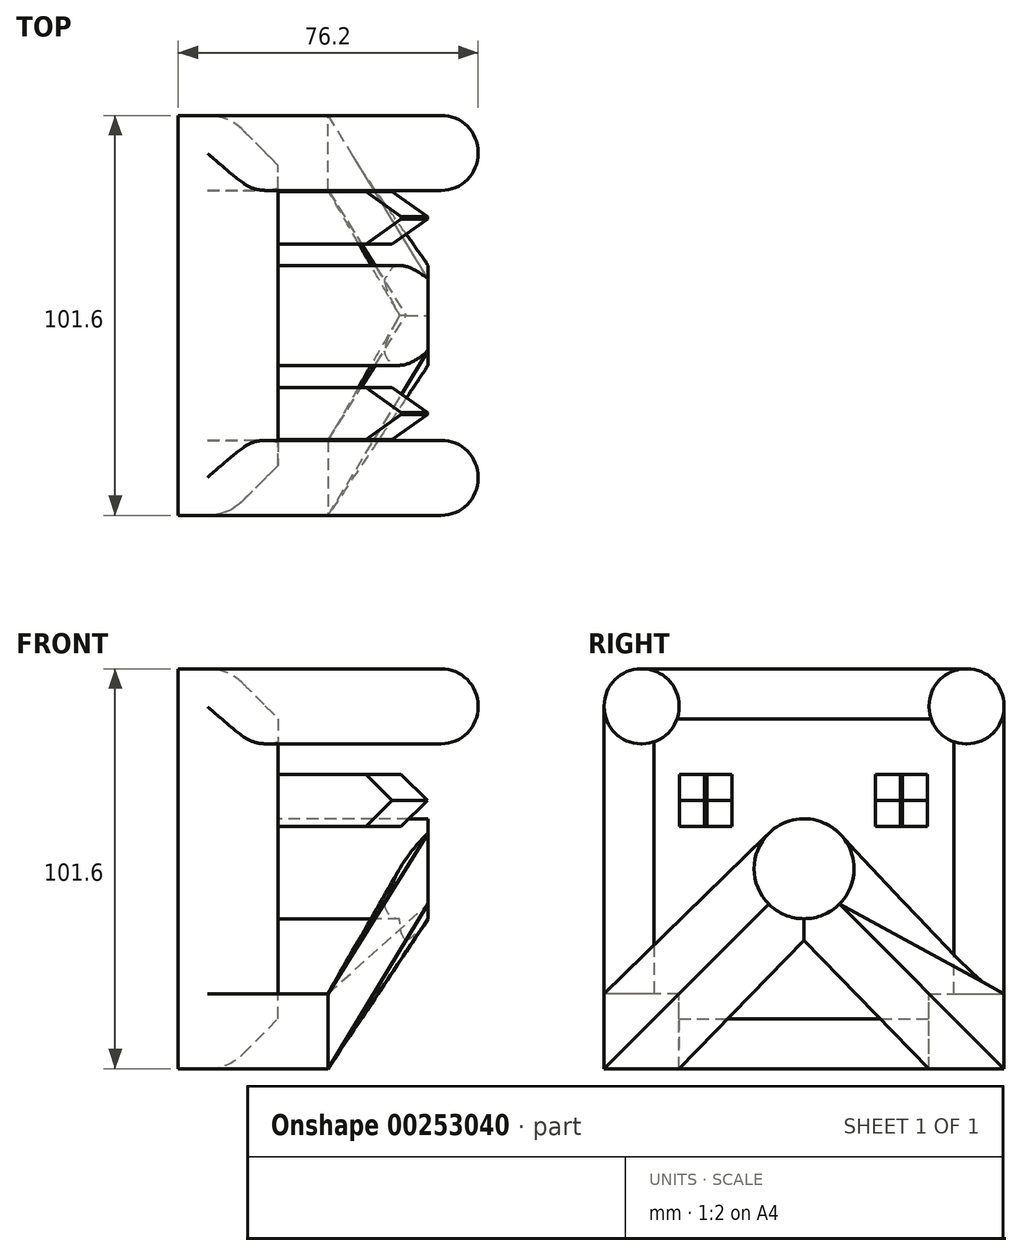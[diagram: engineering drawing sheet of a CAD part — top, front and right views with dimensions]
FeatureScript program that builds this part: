
annotation { "Feature Type Name" : "Feature", "Feature Type Description" : "" }
export const myFeature = defineFeature(function(context is Context, id is Id, definition is map)
    precondition{}
    {
        {
            var Q0;
            Q0=qCreatedBy(makeId("Right.planeOp"),FACE);
            var sketch = newSketch(context, id + "F0", { "sketchPlane" : qUnion([Q0])});
            skLineSegment(sketch, "E0", {"start": v(0, -50.8) * mm, "end": v(50.8, -50.8) * mm});
            skLineSegment(sketch, "E1", {"start": v(50.8, -50.8) * mm, "end": v(-50.8, -50.8) * mm});
            skLineSegment(sketch, "E2", {"start": v(50.8, 50.8) * mm, "end": v(50.8, -50.8) * mm});
            skLineSegment(sketch, "E3", {"start": v(-50.8, 50.8) * mm, "end": v(50.8, 50.8) * mm});
            skLineSegment(sketch, "E4", {"start": v(-50.8, 50.8) * mm, "end": v(-50.8, -50.8) * mm});
            skLineSegment(sketch, "E5", {"start": v(-31.75, -50.8) * mm, "end": v(-31.75, -31.75) * mm});
            skLineSegment(sketch, "E6", {"start": v(-31.75, -31.75) * mm, "end": v(-50.8, -31.75) * mm});
            skLineSegment(sketch, "E7", {"start": v(-31.75, 50.8) * mm, "end": v(-31.75, 31.75) * mm});
            skLineSegment(sketch, "E8", {"start": v(-31.75, 31.75) * mm, "end": v(-50.8, 31.75) * mm});
            skLineSegment(sketch, "E9", {"start": v(50.8, 31.75) * mm, "end": v(31.75, 31.75) * mm});
            skLineSegment(sketch, "E10", {"start": v(31.75, 31.75) * mm, "end": v(31.75, 50.8) * mm});
            skLineSegment(sketch, "E11", {"start": v(31.75, -50.8) * mm, "end": v(31.75, -31.75) * mm});
            skLineSegment(sketch, "E12", {"start": v(31.75, -31.75) * mm, "end": v(50.8, -31.75) * mm});
            skCircle(sketch, "E13", {"center": v(0, 0) * mm, "radius": 12.7 * mm});
            skSolve(sketch);
        }
        {
            var Q0;
            {var subQ5=sQuery(id+"F0.wireOp",EDGE,"E5");Q0=makeQuery(id+"F0.imprint","IMPRINT",FACE,{"disambiguationData":[TD([[makeQuery(id+"F0.imprint","IMPRINT",EDGE,{"derivedFrom":subQ5}),-1.0]])]});}
            extrude(context, id + "F1", {"entities" : qUnion([Q0]), "depth" : 25.4 * mm});
        }
        {
            var Q0;
            {var subQ3=sQuery(id+"F0.wireOp",EDGE,"E7");Q0=makeQuery(id+"F0.imprint","IMPRINT",FACE,{"disambiguationData":[TD([[makeQuery(id+"F0.imprint","IMPRINT",EDGE,{"derivedFrom":subQ3}),-1.0]])]});}
            var Q1;
            {var subQ3=sQuery(id+"F0.wireOp",EDGE,"E9");Q1=makeQuery(id+"F0.imprint","IMPRINT",FACE,{"disambiguationData":[TD([[makeQuery(id+"F0.imprint","IMPRINT",EDGE,{"derivedFrom":subQ3}),-1.0]])]});}
            extrude(context, id + "F2", {"entities" : qUnion([Q0, Q1]), "operationType" : NewBodyOperationType.ADD, "depth" : 76.2 * mm});
        }
        {
            var Q0;
            {var subQ3=sQuery(id+"F0.wireOp",EDGE,"E5");Q0=makeQuery(id+"F0.imprint","IMPRINT",FACE,{"disambiguationData":[TD([[makeQuery(id+"F0.imprint","IMPRINT",EDGE,{"derivedFrom":subQ3}),1.0]])]});}
            var Q1;
            {var subQ3=sQuery(id+"F0.wireOp",EDGE,"E11");Q1=makeQuery(id+"F0.imprint","IMPRINT",FACE,{"disambiguationData":[TD([[makeQuery(id+"F0.imprint","IMPRINT",EDGE,{"derivedFrom":subQ3}),-1.0]])]});}
            extrude(context, id + "F3", {"entities" : qUnion([Q0, Q1]), "operationType" : NewBodyOperationType.ADD, "depth" : 38.1 * mm});
        }
        {
            var Q0;
            Q0=makeQuery(id+"F0.imprint","IMPRINT",FACE,{"disambiguationData":[TD([[makeQuery(id+"F0.imprint","IMPRINT",EDGE,{"derivedFrom":sQuery(id+"F0.wireOp",EDGE,"E13")}),1.0]])]});
            extrude(context, id + "F4", {"entities" : qUnion([Q0]), "operationType" : NewBodyOperationType.ADD, "depth" : 63.5 * mm});
        }
        {
            var Q1;
            Q1=makeQuery(id+"F3.opExtrude","CAP_FACE",FACE,{"disambiguationData":[OSD([sQuery(id+"F0.wireOp",EDGE,"E1"),sQuery(id+"F0.wireOp",EDGE,"E4"),sQuery(id+"F0.wireOp",EDGE,"E5"),sQuery(id+"F0.wireOp",EDGE,"E6")])],"isStart":false});
            var Q2;
            Q2=makeQuery(id+"F4.opExtrude","CAP_FACE",FACE,{"disambiguationData":[OSD([sQuery(id+"F0.wireOp",EDGE,"E13")])],"isStart":false});
            loft(context, id + "F5", {"operationType" : NewBodyOperationType.ADD, "sheetProfilesArray" : [{ "sheetProfileEntities" : qUnion([Q1]) }, { "sheetProfileEntities" : qUnion([Q2]) }]});
        }
        {
            var Q1;
            Q1=makeQuery(id+"F3.opExtrude","CAP_FACE",FACE,{"disambiguationData":[OSD([sQuery(id+"F0.wireOp",EDGE,"E1"),sQuery(id+"F0.wireOp",EDGE,"E2"),sQuery(id+"F0.wireOp",EDGE,"E11"),sQuery(id+"F0.wireOp",EDGE,"E12")])],"isStart":false});
            var Q2;
            Q2=makeQuery(id+"F4.opExtrude","CAP_FACE",FACE,{"disambiguationData":[OSD([sQuery(id+"F0.wireOp",EDGE,"E13")])],"isStart":false});
            loft(context, id + "F6", {"operationType" : NewBodyOperationType.ADD, "sheetProfilesArray" : [{ "sheetProfileEntities" : qUnion([Q1]) }, { "sheetProfileEntities" : qUnion([Q2]) }]});
        }
        {
            var Q0;
            Q0=makeQuery(id+"F2.opExtrude","CAP_EDGE",EDGE,{"disambiguationData":[OSD([sQuery(id+"F0.wireOp",EDGE,"E8")])],"isStart":false});
            fillet(context, id + "F7", {"entities" : qUnion([Q0]), "radius" : 9.4 * mm, "tangentPropagation" : true, "allowEdgeOverflow" : false});
        }
        {
            var Q0;
            {var subQ0=sQuery(id+"F0.wireOp",EDGE,"E3");Q0=makeQuery(id+"F2.opExtrude","CAP_EDGE",EDGE,{"disambiguationData":[OSD([subQ0]),TDD([makeQuery(id+"F0.imprint","IMPRINT",EDGE,{"disambiguationData":[TD([[makeQuery(id+"F0.imprint","INTERSECT",VERTEX,{"derivedFrom":[subQ0,sQuery(id+"F0.wireOp",EDGE,"E4")]}),-1.0]])],"derivedFrom":subQ0})])],"isStart":false});}
            fillet(context, id + "F8", {"entities" : qUnion([Q0]), "radius" : 9.4 * mm, "tangentPropagation" : true, "allowEdgeOverflow" : false});
        }
        {
            var Q0;
            Q0=makeQuery(id+"F7.opFillet","BLEND_EDGE",EDGE,{"blendedFrom":[makeQuery(id+"F2.opExtrude","CAP_EDGE",EDGE,{"disambiguationData":[OSD([sQuery(id+"F0.wireOp",EDGE,"E8")])],"isStart":false}),makeQuery(id+"F2.opExtrude","SWEPT_FACE",FACE,{"disambiguationData":[OSD([sQuery(id+"F0.wireOp",EDGE,"E7")])]})],"blendedInto":[makeQuery(id+"F2.opExtrude","SWEPT_FACE",FACE,{"disambiguationData":[OSD([sQuery(id+"F0.wireOp",EDGE,"E7")])]})]});
            var Q1;
            {var subQ0=sQuery(id+"F0.wireOp",EDGE,"E7");var subQ1=sQuery(id+"F0.wireOp",EDGE,"E3");Q1=makeQuery(id+"F8.opFillet","BLEND_EDGE",EDGE,{"blendedFrom":[makeQuery(id+"F2.opExtrude","CAP_EDGE",EDGE,{"disambiguationData":[OSD([subQ1]),TDD([makeQuery(id+"F0.imprint","IMPRINT",EDGE,{"disambiguationData":[TD([[makeQuery(id+"F0.imprint","INTERSECT",VERTEX,{"derivedFrom":[subQ1,sQuery(id+"F0.wireOp",EDGE,"E4")]}),-1.0]])],"derivedFrom":subQ1})])],"isStart":false}),makeQuery(id+"F2.opExtrude","SWEPT_FACE",FACE,{"disambiguationData":[OSD([subQ0])]})],"blendedInto":[makeQuery(id+"F2.opExtrude","SWEPT_FACE",FACE,{"disambiguationData":[OSD([subQ0])]})]});}
            var Q2;
            {var subQ0=sQuery(id+"F0.wireOp",EDGE,"E4");Q2=makeQuery(id+"F7.opFillet","BLEND_EDGE",EDGE,{"blendedFrom":[makeQuery(id+"F2.opExtrude","CAP_EDGE",EDGE,{"disambiguationData":[OSD([sQuery(id+"F0.wireOp",EDGE,"E8")])],"isStart":false}),makeQuery(id+"F3.boolean.opBoolean","MERGE",FACE,{"derivedFrom":[makeQuery(id+"F2.boolean.opBoolean","MERGE",FACE,{"derivedFrom":[makeQuery(id+"F1.opExtrude","SWEPT_FACE",FACE,{"disambiguationData":[OSD([subQ0])]}),makeQuery(id+"F2.opExtrude","SWEPT_FACE",FACE,{"disambiguationData":[OSD([subQ0])]})]}),makeQuery(id+"F3.opExtrude","SWEPT_FACE",FACE,{"disambiguationData":[OSD([subQ0])]})]})],"blendedInto":[makeQuery(id+"F3.boolean.opBoolean","MERGE",FACE,{"derivedFrom":[makeQuery(id+"F2.boolean.opBoolean","MERGE",FACE,{"derivedFrom":[makeQuery(id+"F1.opExtrude","SWEPT_FACE",FACE,{"disambiguationData":[OSD([subQ0])]}),makeQuery(id+"F2.opExtrude","SWEPT_FACE",FACE,{"disambiguationData":[OSD([subQ0])]})]}),makeQuery(id+"F3.opExtrude","SWEPT_FACE",FACE,{"disambiguationData":[OSD([subQ0])]})]})]});}
            var Q3;
            {var subQ0=sQuery(id+"F0.wireOp",EDGE,"E4");var subQ1=sQuery(id+"F0.wireOp",EDGE,"E3");Q3=makeQuery(id+"F8.opFillet","BLEND_EDGE",EDGE,{"blendedFrom":[makeQuery(id+"F2.opExtrude","CAP_EDGE",EDGE,{"disambiguationData":[OSD([subQ1]),TDD([makeQuery(id+"F0.imprint","IMPRINT",EDGE,{"disambiguationData":[TD([[makeQuery(id+"F0.imprint","INTERSECT",VERTEX,{"derivedFrom":[subQ1,subQ0]}),-1.0]])],"derivedFrom":subQ1})])],"isStart":false}),makeQuery(id+"F3.boolean.opBoolean","MERGE",FACE,{"derivedFrom":[makeQuery(id+"F2.boolean.opBoolean","MERGE",FACE,{"derivedFrom":[makeQuery(id+"F1.opExtrude","SWEPT_FACE",FACE,{"disambiguationData":[OSD([subQ0])]}),makeQuery(id+"F2.opExtrude","SWEPT_FACE",FACE,{"disambiguationData":[OSD([subQ0])]})]}),makeQuery(id+"F3.opExtrude","SWEPT_FACE",FACE,{"disambiguationData":[OSD([subQ0])]})]})],"blendedInto":[makeQuery(id+"F3.boolean.opBoolean","MERGE",FACE,{"derivedFrom":[makeQuery(id+"F2.boolean.opBoolean","MERGE",FACE,{"derivedFrom":[makeQuery(id+"F1.opExtrude","SWEPT_FACE",FACE,{"disambiguationData":[OSD([subQ0])]}),makeQuery(id+"F2.opExtrude","SWEPT_FACE",FACE,{"disambiguationData":[OSD([subQ0])]})]}),makeQuery(id+"F3.opExtrude","SWEPT_FACE",FACE,{"disambiguationData":[OSD([subQ0])]})]})]});}
            fillet(context, id + "F9", {"entities" : qUnion([Q0, Q1, Q2, Q3]), "radius" : 9.4 * mm, "tangentPropagation" : true, "allowEdgeOverflow" : false});
        }
        {
            var Q0;
            Q0=makeQuery(id+"F1.opExtrude","CAP_EDGE",EDGE,{"disambiguationData":[OSD([sQuery(id+"F0.wireOp",EDGE,"E4")])],"isStart":false});
            var Q1;
            Q1=makeQuery(id+"F1.opExtrude","CAP_EDGE",EDGE,{"disambiguationData":[OSD([sQuery(id+"F0.wireOp",EDGE,"E1")])],"isStart":false});
            var Q2;
            Q2=makeQuery(id+"F1.opExtrude","CAP_EDGE",EDGE,{"disambiguationData":[OSD([sQuery(id+"F0.wireOp",EDGE,"E2")])],"isStart":false});
            var Q3;
            Q3=makeQuery(id+"F1.opExtrude","CAP_EDGE",EDGE,{"disambiguationData":[OSD([sQuery(id+"F0.wireOp",EDGE,"E3")])],"isStart":false});
            chamfer(context, id + "F10", {"entities" : qUnion([Q0, Q1, Q2, Q3]), "width" : 12.7 * mm, "tangentPropagation" : true});
        }
        {
            var Q0;
            {var subQ0=sQuery(id+"F0.wireOp",EDGE,"E3");Q0=makeQuery(id+"F10.opChamfer","BLEND_EDGE",EDGE,{"blendedFrom":[makeQuery(id+"F1.opExtrude","CAP_EDGE",EDGE,{"disambiguationData":[OSD([subQ0])],"isStart":false}),makeQuery(id+"F2.boolean.opBoolean","MERGE",FACE,{"derivedFrom":[makeQuery(id+"F1.opExtrude","SWEPT_FACE",FACE,{"disambiguationData":[OSD([subQ0])]}),makeQuery(id+"F2.opExtrude","SWEPT_FACE",FACE,{"disambiguationData":[OSD([subQ0]),TDD([makeQuery(id+"F0.imprint","IMPRINT",EDGE,{"disambiguationData":[TD([[makeQuery(id+"F0.imprint","INTERSECT",VERTEX,{"derivedFrom":[subQ0,sQuery(id+"F0.wireOp",EDGE,"E4")]}),-1.0]])],"derivedFrom":subQ0})])]}),makeQuery(id+"F2.opExtrude","SWEPT_FACE",FACE,{"disambiguationData":[OSD([subQ0]),TDD([makeQuery(id+"F0.imprint","IMPRINT",EDGE,{"disambiguationData":[TD([[makeQuery(id+"F0.imprint","INTERSECT",VERTEX,{"derivedFrom":[sQuery(id+"F0.wireOp",EDGE,"E2"),subQ0]}),1.0]])],"derivedFrom":subQ0})])]})]})],"blendedInto":[makeQuery(id+"F2.boolean.opBoolean","MERGE",FACE,{"derivedFrom":[makeQuery(id+"F1.opExtrude","SWEPT_FACE",FACE,{"disambiguationData":[OSD([subQ0])]}),makeQuery(id+"F2.opExtrude","SWEPT_FACE",FACE,{"disambiguationData":[OSD([subQ0]),TDD([makeQuery(id+"F0.imprint","IMPRINT",EDGE,{"disambiguationData":[TD([[makeQuery(id+"F0.imprint","INTERSECT",VERTEX,{"derivedFrom":[subQ0,sQuery(id+"F0.wireOp",EDGE,"E4")]}),-1.0]])],"derivedFrom":subQ0})])]}),makeQuery(id+"F2.opExtrude","SWEPT_FACE",FACE,{"disambiguationData":[OSD([subQ0]),TDD([makeQuery(id+"F0.imprint","IMPRINT",EDGE,{"disambiguationData":[TD([[makeQuery(id+"F0.imprint","INTERSECT",VERTEX,{"derivedFrom":[sQuery(id+"F0.wireOp",EDGE,"E2"),subQ0]}),1.0]])],"derivedFrom":subQ0})])]})]})]});}
            var Q1;
            {var subQ0=sQuery(id+"F0.wireOp",EDGE,"E4");Q1=makeQuery(id+"F10.opChamfer","BLEND_EDGE",EDGE,{"blendedFrom":[makeQuery(id+"F1.opExtrude","CAP_EDGE",EDGE,{"disambiguationData":[OSD([subQ0])],"isStart":false}),makeQuery(id+"F3.boolean.opBoolean","MERGE",FACE,{"derivedFrom":[makeQuery(id+"F2.boolean.opBoolean","MERGE",FACE,{"derivedFrom":[makeQuery(id+"F1.opExtrude","SWEPT_FACE",FACE,{"disambiguationData":[OSD([subQ0])]}),makeQuery(id+"F2.opExtrude","SWEPT_FACE",FACE,{"disambiguationData":[OSD([subQ0])]})]}),makeQuery(id+"F3.opExtrude","SWEPT_FACE",FACE,{"disambiguationData":[OSD([subQ0])]})]})],"blendedInto":[makeQuery(id+"F3.boolean.opBoolean","MERGE",FACE,{"derivedFrom":[makeQuery(id+"F2.boolean.opBoolean","MERGE",FACE,{"derivedFrom":[makeQuery(id+"F1.opExtrude","SWEPT_FACE",FACE,{"disambiguationData":[OSD([subQ0])]}),makeQuery(id+"F2.opExtrude","SWEPT_FACE",FACE,{"disambiguationData":[OSD([subQ0])]})]}),makeQuery(id+"F3.opExtrude","SWEPT_FACE",FACE,{"disambiguationData":[OSD([subQ0])]})]})]});}
            var Q2;
            {var subQ0=sQuery(id+"F0.wireOp",EDGE,"E1");Q2=makeQuery(id+"F10.opChamfer","BLEND_EDGE",EDGE,{"blendedFrom":[makeQuery(id+"F1.opExtrude","CAP_EDGE",EDGE,{"disambiguationData":[OSD([subQ0])],"isStart":false}),makeQuery(id+"F3.boolean.opBoolean","MERGE",FACE,{"derivedFrom":[makeQuery(id+"F1.opExtrude","SWEPT_FACE",FACE,{"disambiguationData":[OSD([subQ0])]}),makeQuery(id+"F3.opExtrude","SWEPT_FACE",FACE,{"disambiguationData":[OSD([subQ0]),TDD([makeQuery(id+"F0.imprint","IMPRINT",EDGE,{"disambiguationData":[TD([[makeQuery(id+"F0.imprint","INTERSECT",VERTEX,{"derivedFrom":[subQ0,sQuery(id+"F0.wireOp",EDGE,"E2")]}),-1.0]])],"derivedFrom":subQ0})])]}),makeQuery(id+"F3.opExtrude","SWEPT_FACE",FACE,{"disambiguationData":[OSD([subQ0]),TDD([makeQuery(id+"F0.imprint","IMPRINT",EDGE,{"disambiguationData":[TD([[makeQuery(id+"F0.imprint","INTERSECT",VERTEX,{"derivedFrom":[subQ0,sQuery(id+"F0.wireOp",EDGE,"E4")]}),1.0]])],"derivedFrom":subQ0})])]})]})],"blendedInto":[makeQuery(id+"F3.boolean.opBoolean","MERGE",FACE,{"derivedFrom":[makeQuery(id+"F1.opExtrude","SWEPT_FACE",FACE,{"disambiguationData":[OSD([subQ0])]}),makeQuery(id+"F3.opExtrude","SWEPT_FACE",FACE,{"disambiguationData":[OSD([subQ0]),TDD([makeQuery(id+"F0.imprint","IMPRINT",EDGE,{"disambiguationData":[TD([[makeQuery(id+"F0.imprint","INTERSECT",VERTEX,{"derivedFrom":[subQ0,sQuery(id+"F0.wireOp",EDGE,"E2")]}),-1.0]])],"derivedFrom":subQ0})])]}),makeQuery(id+"F3.opExtrude","SWEPT_FACE",FACE,{"disambiguationData":[OSD([subQ0]),TDD([makeQuery(id+"F0.imprint","IMPRINT",EDGE,{"disambiguationData":[TD([[makeQuery(id+"F0.imprint","INTERSECT",VERTEX,{"derivedFrom":[subQ0,sQuery(id+"F0.wireOp",EDGE,"E4")]}),1.0]])],"derivedFrom":subQ0})])]})]})]});}
            var Q3;
            {var subQ0=sQuery(id+"F0.wireOp",EDGE,"E2");Q3=makeQuery(id+"F10.opChamfer","BLEND_EDGE",EDGE,{"blendedFrom":[makeQuery(id+"F1.opExtrude","CAP_EDGE",EDGE,{"disambiguationData":[OSD([subQ0])],"isStart":false}),makeQuery(id+"F3.boolean.opBoolean","MERGE",FACE,{"derivedFrom":[makeQuery(id+"F2.boolean.opBoolean","MERGE",FACE,{"derivedFrom":[makeQuery(id+"F1.opExtrude","SWEPT_FACE",FACE,{"disambiguationData":[OSD([subQ0])]}),makeQuery(id+"F2.opExtrude","SWEPT_FACE",FACE,{"disambiguationData":[OSD([subQ0])]})]}),makeQuery(id+"F3.opExtrude","SWEPT_FACE",FACE,{"disambiguationData":[OSD([subQ0])]})]})],"blendedInto":[makeQuery(id+"F3.boolean.opBoolean","MERGE",FACE,{"derivedFrom":[makeQuery(id+"F2.boolean.opBoolean","MERGE",FACE,{"derivedFrom":[makeQuery(id+"F1.opExtrude","SWEPT_FACE",FACE,{"disambiguationData":[OSD([subQ0])]}),makeQuery(id+"F2.opExtrude","SWEPT_FACE",FACE,{"disambiguationData":[OSD([subQ0])]})]}),makeQuery(id+"F3.opExtrude","SWEPT_FACE",FACE,{"disambiguationData":[OSD([subQ0])]})]})]});}
            fillet(context, id + "F11", {"entities" : qUnion([Q0, Q1, Q2, Q3]), "radius" : 12.7 * mm, "tangentPropagation" : true, "allowEdgeOverflow" : false});
        }
        {
            var Q0;
            Q0=makeQuery(id+"F2.opExtrude","CAP_EDGE",EDGE,{"disambiguationData":[OSD([sQuery(id+"F0.wireOp",EDGE,"E9")])],"isStart":false});
            var Q1;
            {var subQ0=sQuery(id+"F0.wireOp",EDGE,"E3");Q1=makeQuery(id+"F2.opExtrude","CAP_EDGE",EDGE,{"disambiguationData":[OSD([subQ0]),TDD([makeQuery(id+"F0.imprint","IMPRINT",EDGE,{"disambiguationData":[TD([[makeQuery(id+"F0.imprint","INTERSECT",VERTEX,{"derivedFrom":[sQuery(id+"F0.wireOp",EDGE,"E2"),subQ0]}),1.0]])],"derivedFrom":subQ0})])],"isStart":false});}
            fillet(context, id + "F12", {"entities" : qUnion([Q0, Q1]), "radius" : 9.4 * mm, "tangentPropagation" : true, "allowEdgeOverflow" : false});
        }
        {
            var Q0;
            {var subQ0=sQuery(id+"F0.wireOp",EDGE,"E2");Q0=makeQuery(id+"F12.opFillet","BLEND_EDGE",EDGE,{"blendedFrom":[makeQuery(id+"F2.opExtrude","CAP_EDGE",EDGE,{"disambiguationData":[OSD([sQuery(id+"F0.wireOp",EDGE,"E9")])],"isStart":false}),makeQuery(id+"F3.boolean.opBoolean","MERGE",FACE,{"derivedFrom":[makeQuery(id+"F2.boolean.opBoolean","MERGE",FACE,{"derivedFrom":[makeQuery(id+"F1.opExtrude","SWEPT_FACE",FACE,{"disambiguationData":[OSD([subQ0])]}),makeQuery(id+"F2.opExtrude","SWEPT_FACE",FACE,{"disambiguationData":[OSD([subQ0])]})]}),makeQuery(id+"F3.opExtrude","SWEPT_FACE",FACE,{"disambiguationData":[OSD([subQ0])]})]})],"blendedInto":[makeQuery(id+"F3.boolean.opBoolean","MERGE",FACE,{"derivedFrom":[makeQuery(id+"F2.boolean.opBoolean","MERGE",FACE,{"derivedFrom":[makeQuery(id+"F1.opExtrude","SWEPT_FACE",FACE,{"disambiguationData":[OSD([subQ0])]}),makeQuery(id+"F2.opExtrude","SWEPT_FACE",FACE,{"disambiguationData":[OSD([subQ0])]})]}),makeQuery(id+"F3.opExtrude","SWEPT_FACE",FACE,{"disambiguationData":[OSD([subQ0])]})]})]});}
            var Q1;
            {var subQ0=sQuery(id+"F0.wireOp",EDGE,"E2");var subQ1=sQuery(id+"F0.wireOp",EDGE,"E3");Q1=makeQuery(id+"F12.opFillet","BLEND_EDGE",EDGE,{"blendedFrom":[makeQuery(id+"F2.opExtrude","CAP_EDGE",EDGE,{"disambiguationData":[OSD([subQ1]),TDD([makeQuery(id+"F0.imprint","IMPRINT",EDGE,{"disambiguationData":[TD([[makeQuery(id+"F0.imprint","INTERSECT",VERTEX,{"derivedFrom":[subQ0,subQ1]}),1.0]])],"derivedFrom":subQ1})])],"isStart":false}),makeQuery(id+"F3.boolean.opBoolean","MERGE",FACE,{"derivedFrom":[makeQuery(id+"F2.boolean.opBoolean","MERGE",FACE,{"derivedFrom":[makeQuery(id+"F1.opExtrude","SWEPT_FACE",FACE,{"disambiguationData":[OSD([subQ0])]}),makeQuery(id+"F2.opExtrude","SWEPT_FACE",FACE,{"disambiguationData":[OSD([subQ0])]})]}),makeQuery(id+"F3.opExtrude","SWEPT_FACE",FACE,{"disambiguationData":[OSD([subQ0])]})]})],"blendedInto":[makeQuery(id+"F3.boolean.opBoolean","MERGE",FACE,{"derivedFrom":[makeQuery(id+"F2.boolean.opBoolean","MERGE",FACE,{"derivedFrom":[makeQuery(id+"F1.opExtrude","SWEPT_FACE",FACE,{"disambiguationData":[OSD([subQ0])]}),makeQuery(id+"F2.opExtrude","SWEPT_FACE",FACE,{"disambiguationData":[OSD([subQ0])]})]}),makeQuery(id+"F3.opExtrude","SWEPT_FACE",FACE,{"disambiguationData":[OSD([subQ0])]})]})]});}
            var Q2;
            Q2=makeQuery(id+"F12.opFillet","BLEND_EDGE",EDGE,{"blendedFrom":[makeQuery(id+"F2.opExtrude","CAP_EDGE",EDGE,{"disambiguationData":[OSD([sQuery(id+"F0.wireOp",EDGE,"E9")])],"isStart":false}),makeQuery(id+"F2.opExtrude","SWEPT_FACE",FACE,{"disambiguationData":[OSD([sQuery(id+"F0.wireOp",EDGE,"E10")])]})],"blendedInto":[makeQuery(id+"F2.opExtrude","SWEPT_FACE",FACE,{"disambiguationData":[OSD([sQuery(id+"F0.wireOp",EDGE,"E10")])]})]});
            fillet(context, id + "F13", {"entities" : qUnion([Q0, Q1, Q2]), "radius" : 9.4 * mm, "tangentPropagation" : true, "allowEdgeOverflow" : false});
        }
        {
            var Q0;
            Q0=makeQuery(id+"F1.opExtrude","CAP_FACE",FACE,{"disambiguationData":[OSD([sQuery(id+"F0.wireOp",EDGE,"E1"),sQuery(id+"F0.wireOp",EDGE,"E2"),sQuery(id+"F0.wireOp",EDGE,"E3"),sQuery(id+"F0.wireOp",EDGE,"E4"),sQuery(id+"F0.wireOp",EDGE,"E5"),sQuery(id+"F0.wireOp",EDGE,"E6"),sQuery(id+"F0.wireOp",EDGE,"E7"),sQuery(id+"F0.wireOp",EDGE,"E8"),sQuery(id+"F0.wireOp",EDGE,"E9"),sQuery(id+"F0.wireOp",EDGE,"E10"),sQuery(id+"F0.wireOp",EDGE,"E11"),sQuery(id+"F0.wireOp",EDGE,"E12"),sQuery(id+"F0.wireOp",EDGE,"E13")])],"isStart":false});
            var sketch = newSketch(context, id + "F14", { "sketchPlane" : qUnion([Q0])});
            skLineSegment(sketch, "E14.bottom", {"start": v(-18.34, 10.74) * mm, "end": v(-31.62, 10.74) * mm});
            skLineSegment(sketch, "E14.top", {"start": v(-18.34, 24.02) * mm, "end": v(-31.62, 24.02) * mm});
            skLineSegment(sketch, "E14.left", {"start": v(-18.34, 10.74) * mm, "end": v(-18.34, 24.02) * mm});
            skLineSegment(sketch, "E14.right", {"start": v(-31.62, 10.74) * mm, "end": v(-31.62, 24.02) * mm});
            skLineSegment(sketch, "E15.bottom", {"start": v(18.11, 10.74) * mm, "end": v(31.38, 10.74) * mm});
            skLineSegment(sketch, "E15.top", {"start": v(18.11, 24.02) * mm, "end": v(31.38, 24.02) * mm});
            skLineSegment(sketch, "E15.left", {"start": v(18.11, 10.74) * mm, "end": v(18.11, 24.02) * mm});
            skLineSegment(sketch, "E15.right", {"start": v(31.38, 10.74) * mm, "end": v(31.38, 24.02) * mm});
            skSolve(sketch);
        }
        {
            var Q0;
            Q0=makeQuery(id+"F14.imprint","IMPRINT",FACE,{"disambiguationData":[TD([[makeQuery(id+"F14.imprint","IMPRINT",EDGE,{"derivedFrom":sQuery(id+"F14.wireOp",EDGE,"E15.bottom")}),1.0]])]});
            var Q1;
            Q1=makeQuery(id+"F14.imprint","IMPRINT",FACE,{"disambiguationData":[TD([[makeQuery(id+"F14.imprint","IMPRINT",EDGE,{"derivedFrom":sQuery(id+"F14.wireOp",EDGE,"E14.bottom")}),-1.0]])]});
            extrude(context, id + "F15", {"entities" : qUnion([Q0, Q1]), "operationType" : NewBodyOperationType.ADD, "depth" : 38.1 * mm});
        }
        {
            var Q0;
            Q0=makeQuery(id+"F15.opExtrude","CAP_EDGE",EDGE,{"disambiguationData":[OSD([sQuery(id+"F14.wireOp",EDGE,"E14.bottom")])],"isStart":false});
            var Q1;
            Q1=makeQuery(id+"F15.opExtrude","CAP_EDGE",EDGE,{"disambiguationData":[OSD([sQuery(id+"F14.wireOp",EDGE,"E14.top")])],"isStart":false});
            chamfer(context, id + "F16", {"entities" : qUnion([Q0, Q1]), "width" : 6.86 * mm, "tangentPropagation" : true});
        }
        {
            var Q0;
            Q0=makeQuery(id+"F16.opChamfer","BLEND_EDGE",EDGE,{"blendedFrom":[makeQuery(id+"F15.opExtrude","CAP_EDGE",EDGE,{"disambiguationData":[OSD([sQuery(id+"F14.wireOp",EDGE,"E14.bottom")])],"isStart":false}),makeQuery(id+"F15.opExtrude","SWEPT_FACE",FACE,{"disambiguationData":[OSD([sQuery(id+"F14.wireOp",EDGE,"E14.right")])]})],"blendedInto":[makeQuery(id+"F15.opExtrude","SWEPT_FACE",FACE,{"disambiguationData":[OSD([sQuery(id+"F14.wireOp",EDGE,"E14.right")])]})]});
            var Q1;
            Q1=makeQuery(id+"F16.opChamfer","BLEND_EDGE",EDGE,{"blendedFrom":[makeQuery(id+"F15.opExtrude","CAP_EDGE",EDGE,{"disambiguationData":[OSD([sQuery(id+"F14.wireOp",EDGE,"E14.top")])],"isStart":false}),makeQuery(id+"F15.opExtrude","SWEPT_FACE",FACE,{"disambiguationData":[OSD([sQuery(id+"F14.wireOp",EDGE,"E14.right")])]})],"blendedInto":[makeQuery(id+"F15.opExtrude","SWEPT_FACE",FACE,{"disambiguationData":[OSD([sQuery(id+"F14.wireOp",EDGE,"E14.right")])]})]});
            var Q2;
            Q2=makeQuery(id+"F16.opChamfer","BLEND_EDGE",EDGE,{"blendedFrom":[makeQuery(id+"F15.opExtrude","CAP_EDGE",EDGE,{"disambiguationData":[OSD([sQuery(id+"F14.wireOp",EDGE,"E14.top")])],"isStart":false}),makeQuery(id+"F15.opExtrude","SWEPT_FACE",FACE,{"disambiguationData":[OSD([sQuery(id+"F14.wireOp",EDGE,"E14.left")])]})],"blendedInto":[makeQuery(id+"F15.opExtrude","SWEPT_FACE",FACE,{"disambiguationData":[OSD([sQuery(id+"F14.wireOp",EDGE,"E14.left")])]})]});
            var Q3;
            Q3=makeQuery(id+"F16.opChamfer","BLEND_EDGE",EDGE,{"blendedFrom":[makeQuery(id+"F15.opExtrude","CAP_EDGE",EDGE,{"disambiguationData":[OSD([sQuery(id+"F14.wireOp",EDGE,"E14.bottom")])],"isStart":false}),makeQuery(id+"F15.opExtrude","SWEPT_FACE",FACE,{"disambiguationData":[OSD([sQuery(id+"F14.wireOp",EDGE,"E14.left")])]})],"blendedInto":[makeQuery(id+"F15.opExtrude","SWEPT_FACE",FACE,{"disambiguationData":[OSD([sQuery(id+"F14.wireOp",EDGE,"E14.left")])]})]});
            chamfer(context, id + "F17", {"entities" : qUnion([Q0, Q1, Q2, Q3]), "width" : 6.35 * mm, "tangentPropagation" : true});
        }
        {
            var Q0;
            Q0=makeQuery(id+"F15.opExtrude","CAP_EDGE",EDGE,{"disambiguationData":[OSD([sQuery(id+"F14.wireOp",EDGE,"E15.bottom")])],"isStart":false});
            var Q1;
            Q1=makeQuery(id+"F15.opExtrude","CAP_EDGE",EDGE,{"disambiguationData":[OSD([sQuery(id+"F14.wireOp",EDGE,"E15.top")])],"isStart":false});
            chamfer(context, id + "F18", {"entities" : qUnion([Q0, Q1]), "width" : 6.86 * mm, "tangentPropagation" : true});
        }
        {
            var Q0;
            Q0=makeQuery(id+"F18.opChamfer","BLEND_EDGE",EDGE,{"blendedFrom":[makeQuery(id+"F15.opExtrude","CAP_EDGE",EDGE,{"disambiguationData":[OSD([sQuery(id+"F14.wireOp",EDGE,"E15.bottom")])],"isStart":false}),makeQuery(id+"F15.opExtrude","SWEPT_FACE",FACE,{"disambiguationData":[OSD([sQuery(id+"F14.wireOp",EDGE,"E15.right")])]})],"blendedInto":[makeQuery(id+"F15.opExtrude","SWEPT_FACE",FACE,{"disambiguationData":[OSD([sQuery(id+"F14.wireOp",EDGE,"E15.right")])]})]});
            var Q1;
            Q1=makeQuery(id+"F18.opChamfer","BLEND_EDGE",EDGE,{"blendedFrom":[makeQuery(id+"F15.opExtrude","CAP_EDGE",EDGE,{"disambiguationData":[OSD([sQuery(id+"F14.wireOp",EDGE,"E15.top")])],"isStart":false}),makeQuery(id+"F15.opExtrude","SWEPT_FACE",FACE,{"disambiguationData":[OSD([sQuery(id+"F14.wireOp",EDGE,"E15.right")])]})],"blendedInto":[makeQuery(id+"F15.opExtrude","SWEPT_FACE",FACE,{"disambiguationData":[OSD([sQuery(id+"F14.wireOp",EDGE,"E15.right")])]})]});
            var Q2;
            Q2=makeQuery(id+"F18.opChamfer","BLEND_EDGE",EDGE,{"blendedFrom":[makeQuery(id+"F15.opExtrude","CAP_EDGE",EDGE,{"disambiguationData":[OSD([sQuery(id+"F14.wireOp",EDGE,"E15.bottom")])],"isStart":false}),makeQuery(id+"F15.opExtrude","SWEPT_FACE",FACE,{"disambiguationData":[OSD([sQuery(id+"F14.wireOp",EDGE,"E15.left")])]})],"blendedInto":[makeQuery(id+"F15.opExtrude","SWEPT_FACE",FACE,{"disambiguationData":[OSD([sQuery(id+"F14.wireOp",EDGE,"E15.left")])]})]});
            var Q3;
            Q3=makeQuery(id+"F18.opChamfer","BLEND_EDGE",EDGE,{"blendedFrom":[makeQuery(id+"F15.opExtrude","CAP_EDGE",EDGE,{"disambiguationData":[OSD([sQuery(id+"F14.wireOp",EDGE,"E15.top")])],"isStart":false}),makeQuery(id+"F15.opExtrude","SWEPT_FACE",FACE,{"disambiguationData":[OSD([sQuery(id+"F14.wireOp",EDGE,"E15.left")])]})],"blendedInto":[makeQuery(id+"F15.opExtrude","SWEPT_FACE",FACE,{"disambiguationData":[OSD([sQuery(id+"F14.wireOp",EDGE,"E15.left")])]})]});
            chamfer(context, id + "F19", {"entities" : qUnion([Q0, Q1, Q2, Q3]), "width" : 6.35 * mm, "tangentPropagation" : true});
        }
    });
